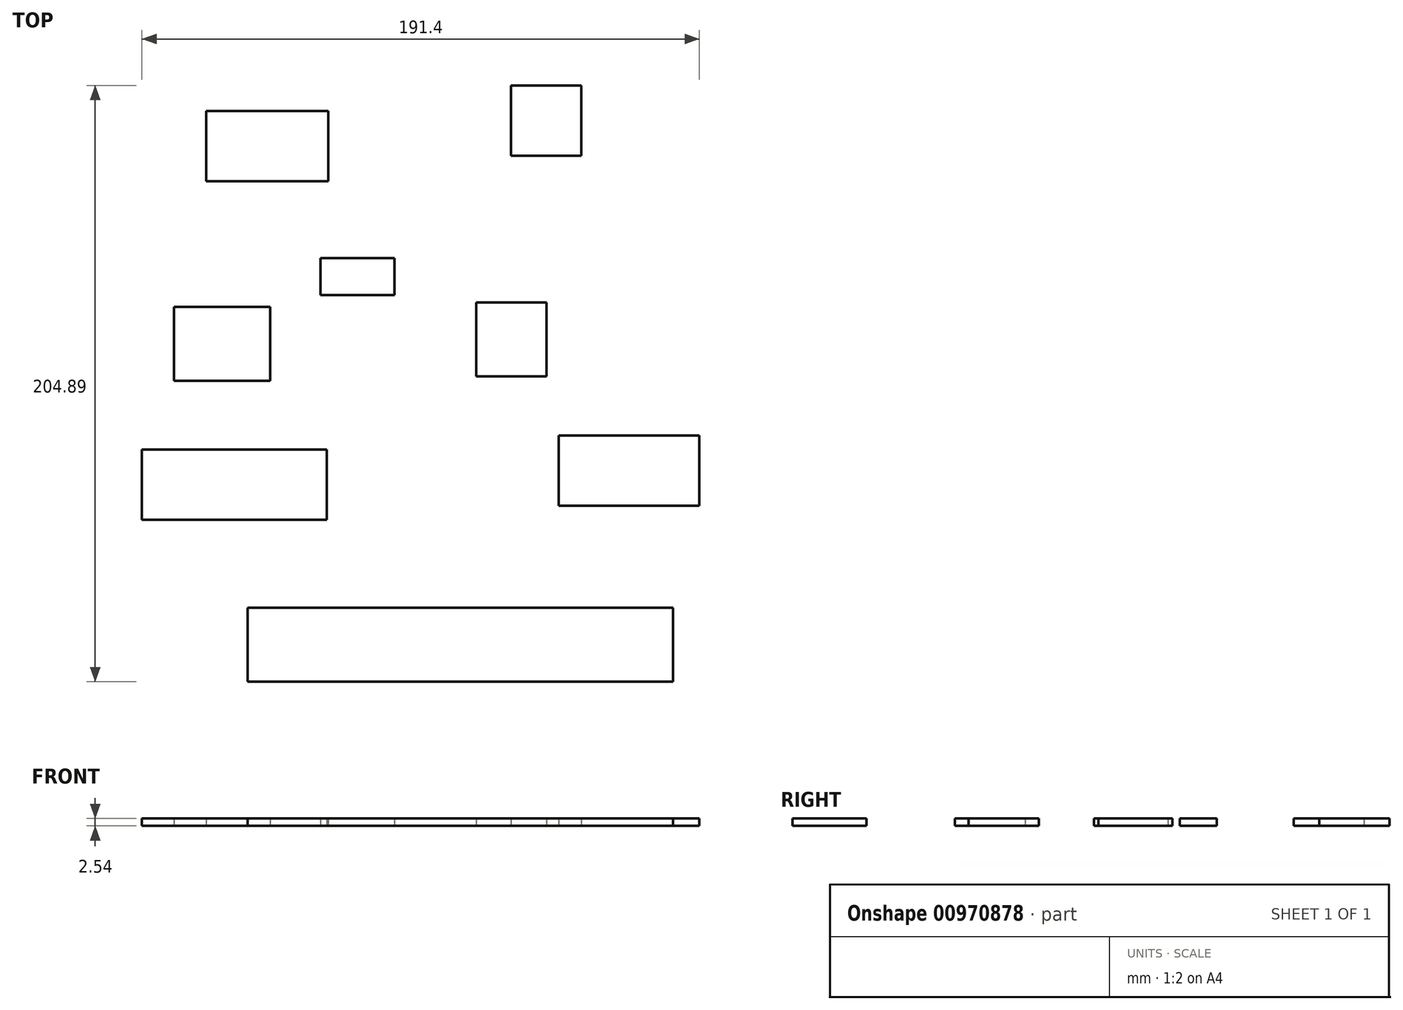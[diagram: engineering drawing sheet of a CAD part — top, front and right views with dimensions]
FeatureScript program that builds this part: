
annotation { "Feature Type Name" : "Feature", "Feature Type Description" : "" }
export const myFeature = defineFeature(function(context is Context, id is Id, definition is map)
    precondition{}
    {
        {
            var Q0;
            Q0=qCreatedBy(makeId("Top.planeOp"),FACE);
            var sketch = newSketch(context, id + "F0", { "sketchPlane" : qUnion([Q0])});
            skLineSegment(sketch, "E0.bottom", {"start": v(-24.02, 0) * mm, "end": v(1.38, 0) * mm});
            skLineSegment(sketch, "E0.top", {"start": v(-24.02, -12.7) * mm, "end": v(1.38, -12.7) * mm});
            skLineSegment(sketch, "E0.left", {"start": v(-24.02, 0) * mm, "end": v(-24.02, -12.7) * mm});
            skLineSegment(sketch, "E0.right", {"start": v(1.38, 0) * mm, "end": v(1.38, -12.7) * mm});
            skSolve(sketch);
        }
        {
            var Q0;
            Q0=qSketchRegion(id+"F0",true);
            extrude(context, id + "F1", {"entities" : qUnion([Q0]), "depth" : 2.54 * mm, "offsetDistance" : 25.4 * mm});
        }
        {
            var Q0;
            Q0=qCreatedBy(makeId("Top.planeOp"),FACE);
            var sketch = newSketch(context, id + "F2", { "sketchPlane" : qUnion([Q0])});
            skLineSegment(sketch, "E1.bottom", {"start": v(41.35, 59.32) * mm, "end": v(65.48, 59.32) * mm});
            skLineSegment(sketch, "E1.top", {"start": v(41.35, 35.2) * mm, "end": v(65.48, 35.2) * mm});
            skLineSegment(sketch, "E1.left", {"start": v(41.35, 59.32) * mm, "end": v(41.35, 35.2) * mm});
            skLineSegment(sketch, "E1.right", {"start": v(65.48, 59.32) * mm, "end": v(65.48, 35.2) * mm});
            skSolve(sketch);
        }
        {
            var Q0;
            Q0=qSketchRegion(id+"F2",true);
            extrude(context, id + "F3", {"entities" : qUnion([Q0]), "depth" : 2.54 * mm, "offsetDistance" : 25.4 * mm});
        }
        {
            var Q0;
            Q0=qCreatedBy(makeId("Top.planeOp"),FACE);
            var sketch = newSketch(context, id + "F4", { "sketchPlane" : qUnion([Q0])});
            skLineSegment(sketch, "E2.bottom", {"start": v(-63.25, 50.6) * mm, "end": v(-21.34, 50.6) * mm});
            skLineSegment(sketch, "E2.top", {"start": v(-63.25, 26.47) * mm, "end": v(-21.34, 26.47) * mm});
            skLineSegment(sketch, "E2.left", {"start": v(-63.25, 50.6) * mm, "end": v(-63.25, 26.47) * mm});
            skLineSegment(sketch, "E2.right", {"start": v(-21.34, 50.6) * mm, "end": v(-21.34, 26.47) * mm});
            skSolve(sketch);
        }
        {
            var Q0;
            Q0=qSketchRegion(id+"F4",true);
            extrude(context, id + "F5", {"entities" : qUnion([Q0]), "depth" : 2.54 * mm, "offsetDistance" : 25.4 * mm});
        }
        {
            var Q0;
            Q0=qCreatedBy(makeId("Top.planeOp"),FACE);
            var sketch = newSketch(context, id + "F6", { "sketchPlane" : qUnion([Q0])});
            skLineSegment(sketch, "E3.bottom", {"start": v(57.83, -61) * mm, "end": v(106.1, -61) * mm});
            skLineSegment(sketch, "E3.top", {"start": v(57.83, -85.13) * mm, "end": v(106.1, -85.13) * mm});
            skLineSegment(sketch, "E3.left", {"start": v(57.83, -61) * mm, "end": v(57.83, -85.13) * mm});
            skLineSegment(sketch, "E3.right", {"start": v(106.1, -61) * mm, "end": v(106.1, -85.13) * mm});
            skSolve(sketch);
        }
        {
            var Q0;
            Q0=qSketchRegion(id+"F6",true);
            extrude(context, id + "F7", {"entities" : qUnion([Q0]), "depth" : 2.54 * mm, "offsetDistance" : 25.4 * mm});
        }
        {
            var Q0;
            Q0=qCreatedBy(makeId("Top.planeOp"),FACE);
            var sketch = newSketch(context, id + "F8", { "sketchPlane" : qUnion([Q0])});
            skLineSegment(sketch, "E4.bottom", {"start": v(-85.31, -65.75) * mm, "end": v(-21.81, -65.75) * mm});
            skLineSegment(sketch, "E4.top", {"start": v(-85.31, -89.88) * mm, "end": v(-21.81, -89.88) * mm});
            skLineSegment(sketch, "E4.left", {"start": v(-85.31, -65.75) * mm, "end": v(-85.31, -89.88) * mm});
            skLineSegment(sketch, "E4.right", {"start": v(-21.81, -65.75) * mm, "end": v(-21.81, -89.88) * mm});
            skSolve(sketch);
        }
        {
            var Q0;
            Q0=qSketchRegion(id+"F8",true);
            extrude(context, id + "F9", {"entities" : qUnion([Q0]), "depth" : 2.54 * mm, "offsetDistance" : 25.4 * mm});
        }
        {
            var Q0;
            Q0=qCreatedBy(makeId("Top.planeOp"),FACE);
            var sketch = newSketch(context, id + "F10", { "sketchPlane" : qUnion([Q0])});
            skLineSegment(sketch, "E5.bottom", {"start": v(29.42, -15.2) * mm, "end": v(53.55, -15.2) * mm});
            skLineSegment(sketch, "E5.top", {"start": v(29.42, -40.6) * mm, "end": v(53.55, -40.6) * mm});
            skLineSegment(sketch, "E5.left", {"start": v(29.42, -15.2) * mm, "end": v(29.42, -40.6) * mm});
            skLineSegment(sketch, "E5.right", {"start": v(53.55, -15.2) * mm, "end": v(53.55, -40.6) * mm});
            skSolve(sketch);
        }
        {
            var Q0;
            Q0=qSketchRegion(id+"F10",true);
            extrude(context, id + "F11", {"entities" : qUnion([Q0]), "depth" : 2.54 * mm, "offsetDistance" : 25.4 * mm});
        }
        {
            var Q0;
            Q0=qCreatedBy(makeId("Top.planeOp"),FACE);
            var sketch = newSketch(context, id + "F12", { "sketchPlane" : qUnion([Q0])});
            skLineSegment(sketch, "E6.bottom", {"start": v(-74.26, -16.7) * mm, "end": v(-41.24, -16.7) * mm});
            skLineSegment(sketch, "E6.top", {"start": v(-74.26, -42.1) * mm, "end": v(-41.24, -42.1) * mm});
            skLineSegment(sketch, "E6.left", {"start": v(-74.26, -16.7) * mm, "end": v(-74.26, -42.1) * mm});
            skLineSegment(sketch, "E6.right", {"start": v(-41.24, -16.7) * mm, "end": v(-41.24, -42.1) * mm});
            skSolve(sketch);
        }
        {
            var Q0;
            Q0=qSketchRegion(id+"F12",true);
            extrude(context, id + "F13", {"entities" : qUnion([Q0]), "depth" : 2.54 * mm, "offsetDistance" : 25.4 * mm});
        }
        {
            var Q0;
            Q0=qCreatedBy(makeId("Top.planeOp"),FACE);
            var sketch = newSketch(context, id + "F14", { "sketchPlane" : qUnion([Q0])});
            skLineSegment(sketch, "E7.bottom", {"start": v(-49.02, -120.17) * mm, "end": v(97.03, -120.17) * mm});
            skLineSegment(sketch, "E7.top", {"start": v(-49.02, -145.57) * mm, "end": v(97.03, -145.57) * mm});
            skLineSegment(sketch, "E7.left", {"start": v(-49.02, -120.17) * mm, "end": v(-49.02, -145.57) * mm});
            skLineSegment(sketch, "E7.right", {"start": v(97.03, -120.17) * mm, "end": v(97.03, -145.57) * mm});
            skSolve(sketch);
        }
        {
            var Q0;
            Q0=qSketchRegion(id+"F14",true);
            extrude(context, id + "F15", {"entities" : qUnion([Q0]), "depth" : 2.54 * mm, "offsetDistance" : 25.4 * mm});
        }
    });
